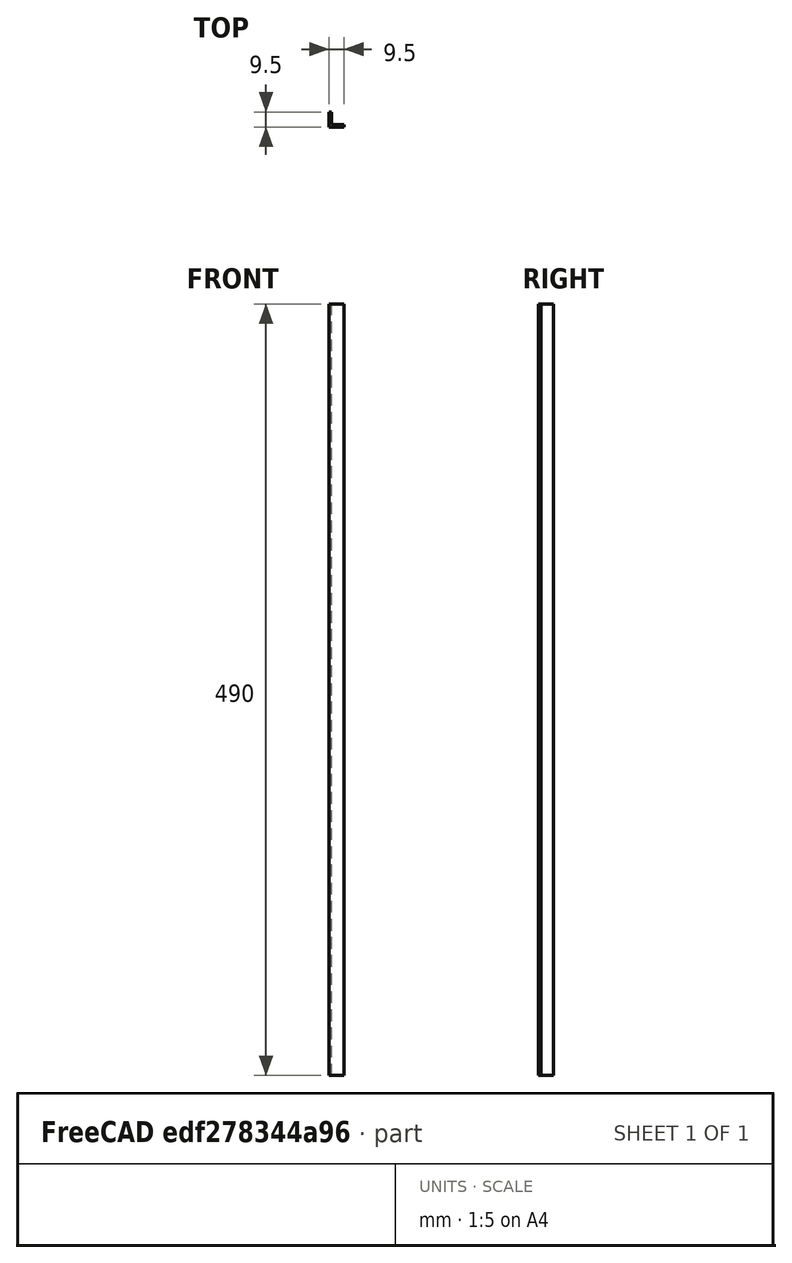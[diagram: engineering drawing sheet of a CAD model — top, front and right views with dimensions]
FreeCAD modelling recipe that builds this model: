
FCSTD DOCUMENT  (FreeCAD 0.21R33668 +7 (Git))
Label: L-back
License: All rights reserved
LicenseURL: http://en.wikipedia.org/wiki/All_rights_reserved
objects: Sketcher::SketchObject×1, PartDesign::Pad×1, PartDesign::Body×1, PartDesign::CoordinateSystem×1, App::Part×1
note: 5 computed .brp shape members not serialized (recipe doc carries the construction recipe); baked Part::Feature solids carry a one-line shape summary decoded from their .brp
EXTERNAL_REF file=planB.FCStd obj=Spreadsheet

FEATURE [Sketcher::SketchObject] Sketch
  FullyConstrained = true
  MapMode = 5
  Support = -> [XY_Plane]
  expr: Constraints[14] = planB#<<data>>.L_thickness
  expr: Constraints[16] = planB#<<data>>.L_size
  sketch-geometry (6):
    g0: LineSegment StartX=0 StartY=0 StartZ=0 EndX=0 EndY=9.5 EndZ=0
    g1: LineSegment StartX=0 StartY=9.5 StartZ=0 EndX=1.6 EndY=9.5 EndZ=0
    g2: LineSegment StartX=1.6 StartY=9.5 StartZ=0 EndX=1.6 EndY=1.6 EndZ=0
    g3: LineSegment StartX=1.6 StartY=1.6 StartZ=0 EndX=9.5 EndY=1.6 EndZ=0
    g4: LineSegment StartX=9.5 StartY=1.6 StartZ=0 EndX=9.5 EndY=0 EndZ=0
    g5: LineSegment StartX=9.5 StartY=0 StartZ=0 EndX=0 EndY=0 EndZ=0
  constraints (17):
    c: Coincident(g-1,g0)
    c: PointOnObject(g0,g-2)
    c: Coincident(g0,g1)
    c: Horizontal(g1)
    c: Coincident(g1,g2)
    c: Vertical(g2)
    c: Coincident(g2,g3)
    c: Horizontal(g3)
    c: Coincident(g3,g4)
    c: PointOnObject(g4,g-1)
    c: Vertical(g4)
    c: Coincident(g4,g5)
    c: Coincident(g5,g0)
    c: Equal(g4,g1)
    c: Distance(g1) = 1.6
    c: Equal(g0,g5)
    c: Distance(g0) = 9.5
FEATURE [PartDesign::Pad] Pad
  Direction = (0,0,1)
  Length = 490
  Length2 = 10
  Profile = -> Sketch
  ReferenceAxis = -> Sketch [N_Axis]
  Type = 0
  expr: Length = planB#<<data>>.case_w - 10
FEATURE [PartDesign::Body] Body
  Group = -> [Sketch,Pad]
  Origin = -> Origin
  Tip = -> Pad
FEATURE [PartDesign::CoordinateSystem] LCS_0
  AttacherType = Attacher::AttachEngine3D
  MapMode = 2
  Support = -> [X_Axis001]
FEATURE [App::Part] L_back
  Group = -> [LCS_0,Body]
  Origin = -> Origin001
